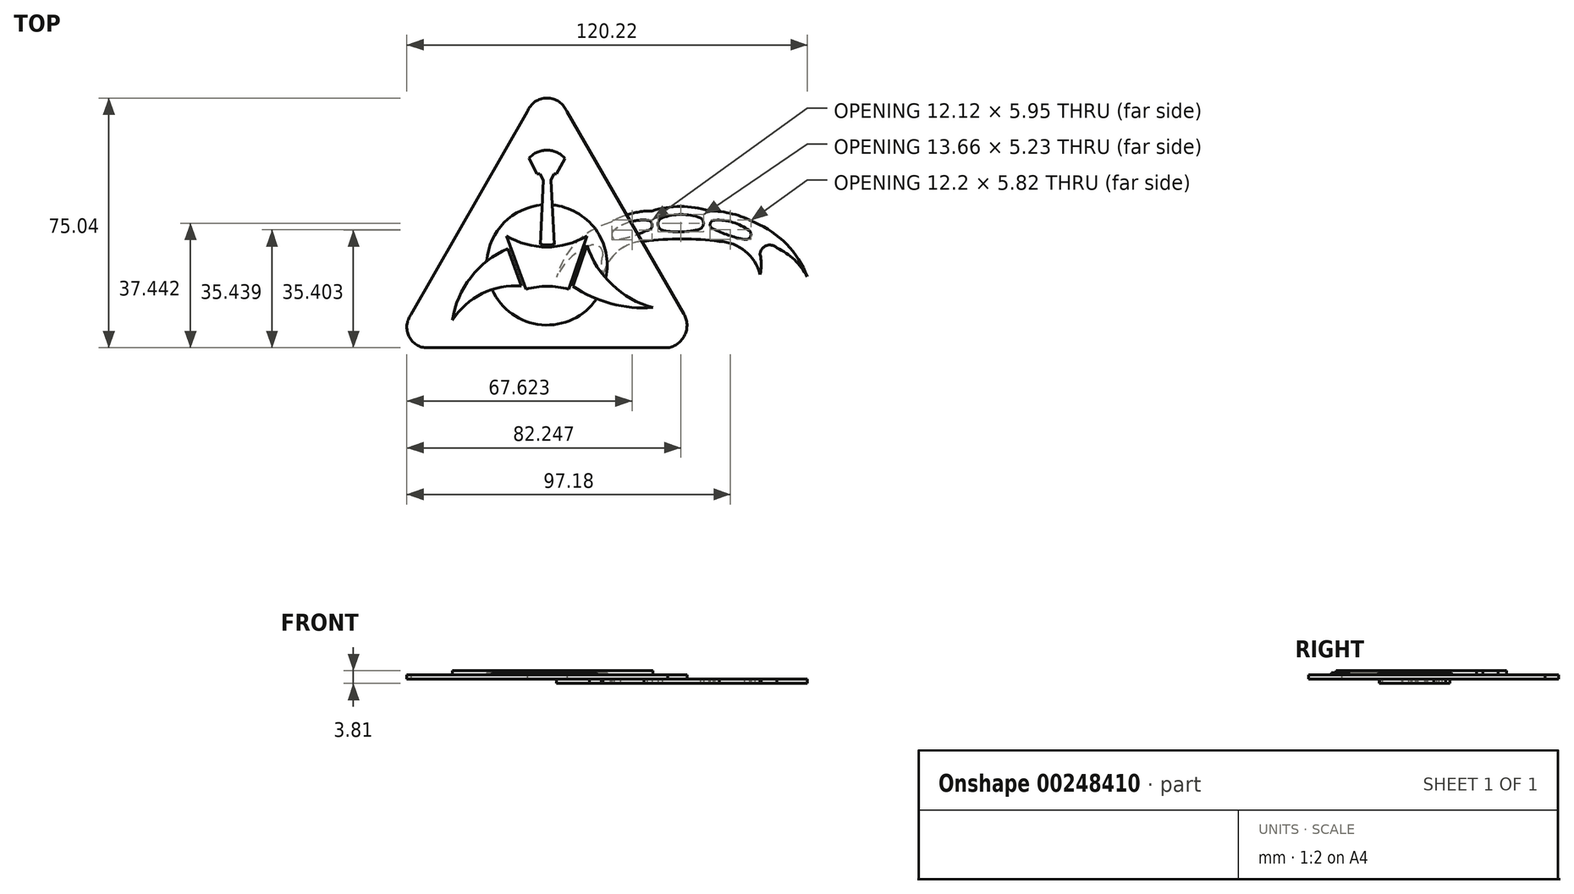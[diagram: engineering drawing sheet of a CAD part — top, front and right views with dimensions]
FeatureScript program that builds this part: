
annotation { "Feature Type Name" : "Feature", "Feature Type Description" : "" }
export const myFeature = defineFeature(function(context is Context, id is Id, definition is map)
    precondition{}
    {
        {
            var Q0;
            Q0=qCreatedBy(makeId("Top.planeOp"),FACE);
            var sketch = newSketch(context, id + "F0", { "sketchPlane" : qUnion([Q0])});
            skArc(sketch, "E0", {"start": v(-21.29, 4) * mm, "mid": v(-31.54, -2.08) * mm, "end": v(-37.43, -12.45) * mm});
            skArc(sketch, "E1", {"start": v(-8.76, 7.5) * mm, "mid": v(-15.27, 6.64) * mm, "end": v(-21.29, 4) * mm});
            skArc(sketch, "E2", {"start": v(8.32, 7.5) * mm, "mid": v(-0.22, 8.8) * mm, "end": v(-8.76, 7.5) * mm});
            skArc(sketch, "E3", {"start": v(22.08, 4) * mm, "mid": v(15.42, 6.62) * mm, "end": v(8.32, 7.5) * mm});
            skArc(sketch, "E4", {"start": v(37.85, -12.23) * mm, "mid": v(31.64, -2.49) * mm, "end": v(22.08, 4) * mm});
            skPoint(sketch, "E5.endSnap0", {"position": v(-23.41, -6.51) * mm});
            skArc(sketch, "E6", {"start": v(11.5, -1.63) * mm, "mid": v(0.2, -0.9) * mm, "end": v(-11.11, -1.63) * mm});
            skArc(sketch, "E7", {"start": v(23.68, -11.56) * mm, "mid": v(19.23, -4.59) * mm, "end": v(11.5, -1.63) * mm});
            skArc(sketch, "E8", {"start": v(37.85, -12.23) * mm, "mid": v(34, -7.2) * mm, "end": v(28.75, -3.64) * mm});
            skArc(sketch, "E9", {"start": v(28.75, -3.64) * mm, "mid": v(25.61, -2.91) * mm, "end": v(23.68, -5.5) * mm});
            skArc(sketch, "E10", {"start": v(23.68, -11.56) * mm, "mid": v(24.05, -8.53) * mm, "end": v(23.68, -5.5) * mm});
            skArc(sketch, "E11", {"start": v(-18.27, -0.86) * mm, "mid": v(-14.18, 0.07) * mm, "end": v(-10.28, 1.63) * mm});
            skArc(sketch, "E12", {"start": v(-10.28, 4.71) * mm, "mid": v(-15.5, 4.15) * mm, "end": v(-20.14, 1.67) * mm});
            skArc(sketch, "E13", {"start": v(-10.28, 1.63) * mm, "mid": v(-8.69, 3.17) * mm, "end": v(-10.28, 4.71) * mm});
            skArc(sketch, "E14", {"start": v(-20.14, 1.67) * mm, "mid": v(-20.52, -0.57) * mm, "end": v(-18.27, -0.86) * mm});
            skArc(sketch, "E15", {"start": v(5.74, 5.46) * mm, "mid": v(0, 6.44) * mm, "end": v(-5.75, 5.42) * mm});
            skArc(sketch, "E16", {"start": v(-5.33, 1.63) * mm, "mid": v(0.23, 1.23) * mm, "end": v(5.74, 2.1) * mm});
            skArc(sketch, "E17", {"start": v(-5.75, 5.42) * mm, "mid": v(-6.95, 3.37) * mm, "end": v(-5.33, 1.63) * mm});
            skArc(sketch, "E18", {"start": v(5.74, 2.1) * mm, "mid": v(6.7, 3.78) * mm, "end": v(5.74, 5.46) * mm});
            skArc(sketch, "E19", {"start": v(20.41, 1.63) * mm, "mid": v(15.52, 4.07) * mm, "end": v(10.1, 4.71) * mm});
            skArc(sketch, "E20", {"start": v(9.57, 2.1) * mm, "mid": v(14.16, 0.22) * mm, "end": v(18.96, -1.04) * mm});
            skArc(sketch, "E21", {"start": v(10.1, 4.71) * mm, "mid": v(8.72, 3.63) * mm, "end": v(9.57, 2.1) * mm});
            skArc(sketch, "E22", {"start": v(18.96, -1.04) * mm, "mid": v(20.74, -0.28) * mm, "end": v(20.41, 1.63) * mm});
            skArc(sketch, "E23", {"start": v(-11.11, -1.63) * mm, "mid": v(-18.92, -4.53) * mm, "end": v(-23.41, -11.56) * mm});
            skArc(sketch, "E24", {"start": v(-27.54, -3) * mm, "mid": v(-33.4, -6.78) * mm, "end": v(-37.43, -12.45) * mm});
            skArc(sketch, "E25", {"start": v(-23.5, -5.64) * mm, "mid": v(-24.72, -3.1) * mm, "end": v(-27.54, -3) * mm});
            skArc(sketch, "E26", {"start": v(-23.5, -5.64) * mm, "mid": v(-23.98, -8.6) * mm, "end": v(-23.41, -11.56) * mm});
            skSolve(sketch);
        }
        {
            var Q0;
            Q0 = qSketchRegion(id + "F0", true);
            extrude(context, id + "F1", {"entities" : qUnion([Q0]), "depth" : 1.27 * mm});
        }
        {
            var Q0;
            Q0=qCreatedBy(makeId("Top.planeOp"),FACE);
            cPlane(context, id + "F2", {"entities" : qUnion([Q0]), "cplaneType" : CPlaneType.OFFSET, "offset" : 1.27 * mm, "width" : 152.4 * mm, "height" : 152.4 * mm});
        }
        {
            var Q0;
            Q0=qCreatedBy(id+"F2.planeOp",FACE);
            var sketch = newSketch(context, id + "F3", { "sketchPlane" : qUnion([Q0])});
            skLineSegment(sketch, "E27", {"start": v(-46.2, 37.34) * mm, "end": v(-81.1, -23.66) * mm});
            skLineSegment(sketch, "E28", {"start": v(-34.33, 37.34) * mm, "end": v(0.82, -23.4) * mm});
            skLineSegment(sketch, "E29", {"start": v(-76.18, -33.62) * mm, "end": v(-3.99, -33.62) * mm});
            skArc(sketch, "E30", {"start": v(-81.1, -23.66) * mm, "mid": v(-81.73, -30.17) * mm, "end": v(-76.18, -33.62) * mm});
            skArc(sketch, "E31", {"start": v(-3.99, -33.62) * mm, "mid": v(1.1, -29.78) * mm, "end": v(0.82, -23.4) * mm});
            skArc(sketch, "E32", {"start": v(-34.33, 37.34) * mm, "mid": v(-40.27, 41.42) * mm, "end": v(-46.2, 37.34) * mm});
            skSolve(sketch);
        }
        {
            var Q0;
            Q0 = qSketchRegion(id + "F3", true);
            extrude(context, id + "F4", {"entities" : qUnion([Q0]), "depth" : 1.27 * mm});
        }
        {
            var Q0;
            Q0=makeQuery(id+"F4.opExtrude","CAP_FACE",FACE,{"disambiguationData":[OSD([sQuery(id+"F3.wireOp",EDGE,"E27"),sQuery(id+"F3.wireOp",EDGE,"E28"),sQuery(id+"F3.wireOp",EDGE,"E29"),sQuery(id+"F3.wireOp",EDGE,"E30"),sQuery(id+"F3.wireOp",EDGE,"E31"),sQuery(id+"F3.wireOp",EDGE,"E32")])],"isStart":false});
            var sketch = newSketch(context, id + "F5", { "sketchPlane" : qUnion([Q0])});
            skLineSegment(sketch, "E33", {"start": v(-45.7, 23.35) * mm, "end": v(-43.35, 18.65) * mm});
            skLineSegment(sketch, "E34", {"start": v(-43.35, 18.65) * mm, "end": v(-42.43, 18.65) * mm});
            skLineSegment(sketch, "E35", {"start": v(-37.4, 18.65) * mm, "end": v(-34.93, 23.27) * mm});
            skArc(sketch, "E36", {"start": v(-34.93, 23.27) * mm, "mid": v(-40.3, 25.77) * mm, "end": v(-45.7, 23.35) * mm});
            skLineSegment(sketch, "E37", {"start": v(-42.43, 18.65) * mm, "end": v(-41.33, 16.73) * mm});
            skLineSegment(sketch, "E38", {"start": v(-41.33, 16.73) * mm, "end": v(-42.3, -2.53) * mm});
            skLineSegment(sketch, "E39", {"start": v(-38.05, -2.53) * mm, "end": v(-39.04, 16.73) * mm});
            skLineSegment(sketch, "E40", {"start": v(-39.04, 16.73) * mm, "end": v(-38.2, 18.65) * mm});
            skArc(sketch, "E41", {"start": v(-42.3, -2.53) * mm, "mid": v(-40.17, -2.75) * mm, "end": v(-38.05, -2.53) * mm});
            skArc(sketch, "E42", {"start": v(-52.4, 0) * mm, "mid": v(-40.35, -3.34) * mm, "end": v(-28.3, 0) * mm});
            skLineSegment(sketch, "E43", {"start": v(-52.4, 0) * mm, "end": v(-46.58, -16) * mm});
            skLineSegment(sketch, "E44", {"start": v(-33.79, -16) * mm, "end": v(-28.3, 0) * mm});
            skLineSegment(sketch, "E45", {"start": v(-28.3, -2.82) * mm, "end": v(-32.5, -15.1) * mm});
            skLineSegment(sketch, "E46", {"start": v(-52.08, -3.8) * mm, "end": v(-47.98, -15.04) * mm});
            skArc(sketch, "E47", {"start": v(-33.79, -16) * mm, "mid": v(-40.19, -15.15) * mm, "end": v(-46.58, -16) * mm});
            skArc(sketch, "E48", {"start": v(-52.08, -3.8) * mm, "mid": v(-63.15, -12.44) * mm, "end": v(-68.7, -25.35) * mm});
            skArc(sketch, "E49", {"start": v(-47.98, -15.04) * mm, "mid": v(-59.75, -17.36) * mm, "end": v(-68.7, -25.35) * mm});
            skArc(sketch, "E50", {"start": v(-28.3, -2.82) * mm, "mid": v(-20.74, -14.67) * mm, "end": v(-8.49, -21.55) * mm});
            skArc(sketch, "E51", {"start": v(-32.5, -15.1) * mm, "mid": v(-21.04, -20.35) * mm, "end": v(-8.49, -21.55) * mm});
            skLineSegment(sketch, "E52.trimOffspring", {"start": v(-38.2, 18.65) * mm, "end": v(-37.4, 18.65) * mm});
            skPoint(sketch, "E53.startSnap0", {"position": v(-40.3, 25.77) * mm});
            skPoint(sketch, "E53.start.orphan", {"position": v(-40.3, 41.41) * mm});
            skArc(sketch, "E54", {"start": v(-56.78, -16.13) * mm, "mid": v(-41.89, -26.72) * mm, "end": v(-25.37, -18.9) * mm});
            skArc(sketch, "E55.trimOffspring", {"start": v(-22.66, -12.67) * mm, "mid": v(-25.69, 1.94) * mm, "end": v(-38.66, 9.3) * mm});
            skArc(sketch, "E56.trimOffspring", {"start": v(-41.7, 9.31) * mm, "mid": v(-53.17, 3.98) * mm, "end": v(-58.34, -7.56) * mm});
            skSolve(sketch);
        }
        {
            var Q0;
            Q0=makeQuery(id+"F5.imprint","IMPRINT",FACE,{"disambiguationData":[TD([[makeQuery(id+"F5.imprint","IMPRINT",EDGE,{"derivedFrom":sQuery(id+"F5.wireOp",EDGE,"E33")}),1.0]])]});
            var Q1;
            {var subQ1=sQuery(id+"F5.wireOp",EDGE,"E45");Q1=makeQuery(id+"F5.imprint","IMPRINT",FACE,{"disambiguationData":[TD([[makeQuery(id+"F5.imprint","IMPRINT",EDGE,{"derivedFrom":subQ1}),1.0]])]});}
            var Q2;
            {var subQ1=sQuery(id+"F5.wireOp",EDGE,"E46");Q2=makeQuery(id+"F5.imprint","IMPRINT",FACE,{"disambiguationData":[TD([[makeQuery(id+"F5.imprint","IMPRINT",EDGE,{"derivedFrom":subQ1}),-1.0]])]});}
            var Q3;
            Q3=makeQuery(id+"F5.imprint","IMPRINT",FACE,{"disambiguationData":[TD([[makeQuery(id+"F5.imprint","IMPRINT",EDGE,{"derivedFrom":sQuery(id+"F5.wireOp",EDGE,"E42")}),-1.0]])]});
            extrude(context, id + "F6", {"entities" : qUnion([Q0, Q1, Q2, Q3]), "operationType" : NewBodyOperationType.ADD, "depth" : 1.27 * mm});
        }
        {
            var Q0;
            {var subQ6=sQuery(id+"F5.wireOp",EDGE,"E41");Q0=makeQuery(id+"F5.imprint","IMPRINT",FACE,{"disambiguationData":[TD([[makeQuery(id+"F5.imprint","IMPRINT",EDGE,{"derivedFrom":subQ6}),-1.0]])]});}
            extrude(context, id + "F7", {"entities" : qUnion([Q0]), "operationType" : NewBodyOperationType.ADD, "depth" : 0.64 * mm});
        }
    });
